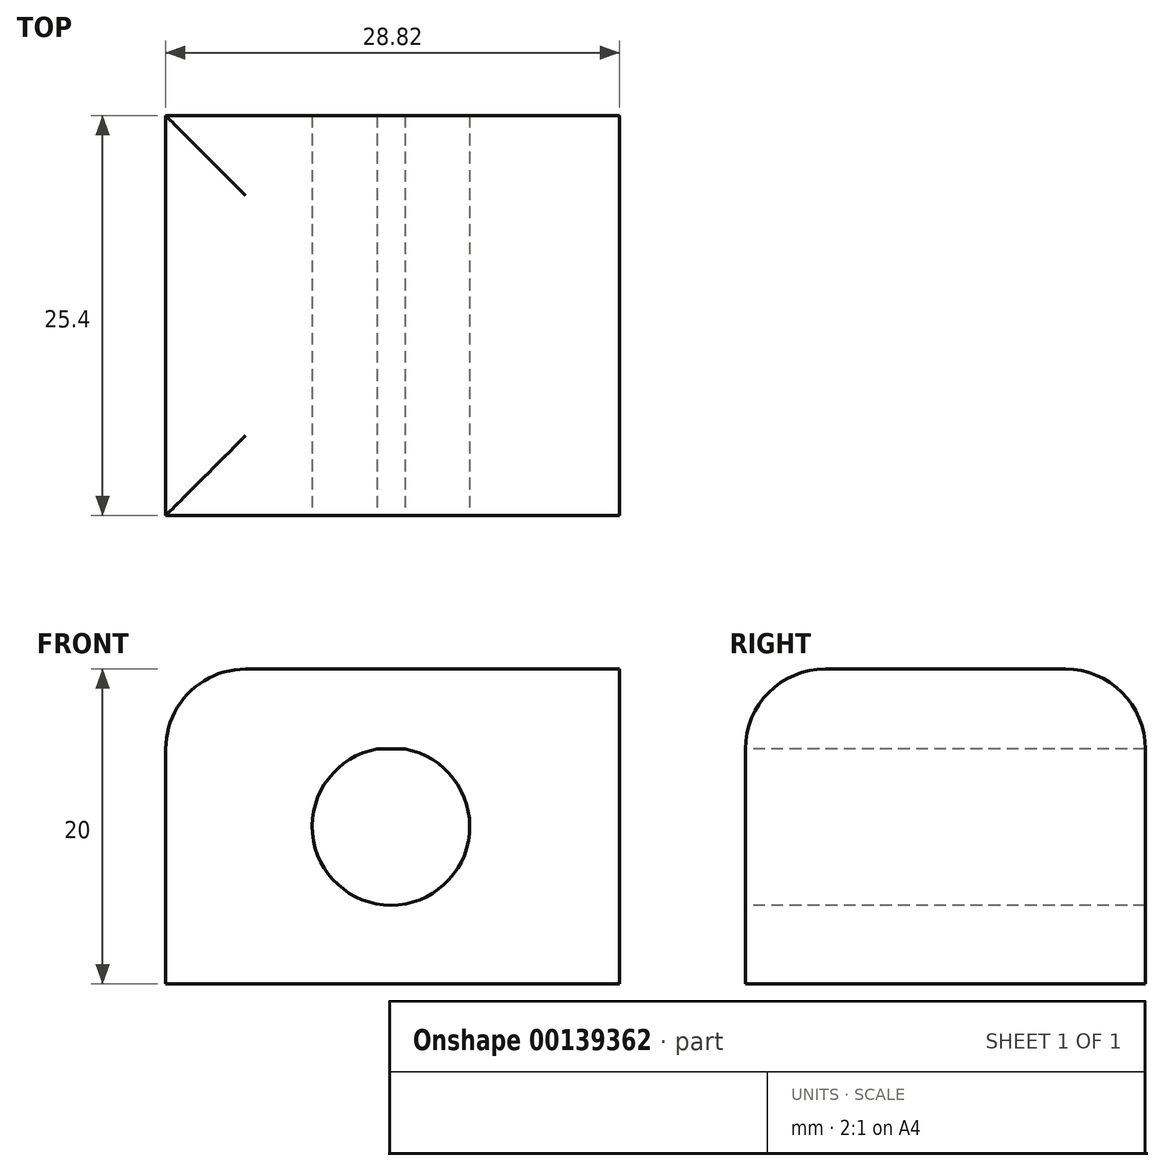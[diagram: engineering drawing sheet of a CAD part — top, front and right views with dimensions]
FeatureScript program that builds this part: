
annotation { "Feature Type Name" : "Feature", "Feature Type Description" : "" }
export const myFeature = defineFeature(function(context is Context, id is Id, definition is map)
    precondition{}
    {
        {
            var Q0;
            Q0=qCreatedBy(makeId("Front.planeOp"),FACE);
            var sketch = newSketch(context, id + "F0", { "sketchPlane" : qUnion([Q0])});
            skLineSegment(sketch, "E0.bottom", {"start": v(14.41, -10) * mm, "end": v(-14.41, -10) * mm});
            skLineSegment(sketch, "E0.top", {"start": v(14.41, 10) * mm, "end": v(-14.41, 10) * mm});
            skLineSegment(sketch, "E0.left", {"start": v(14.41, -10) * mm, "end": v(14.41, 10) * mm});
            skLineSegment(sketch, "E0.right", {"start": v(-14.41, -10) * mm, "end": v(-14.41, 10) * mm});
            skPoint(sketch, "E0.middle", {"position": v(0, 0) * mm});
            skSolve(sketch);
        }
        {
            var Q0;
            Q0=makeQuery(id+"F0.imprint","IMPRINT",FACE,{"disambiguationData":[TD([[makeQuery(id+"F0.imprint","IMPRINT",EDGE,{"derivedFrom":sQuery(id+"F0.wireOp",EDGE,"E0.bottom")}),-1.0]])]});
            extrude(context, id + "F1", {"entities" : qUnion([Q0]), "depth" : 25.4 * mm});
        }
        {
            var Q0;
            Q0=makeQuery(id+"F1.opExtrude","CAP_EDGE",EDGE,{"disambiguationData":[OSD([sQuery(id+"F0.wireOp",EDGE,"E0.top")])],"isStart":true});
            var Q1;
            Q1=makeQuery(id+"F1.opExtrude","SWEPT_EDGE",EDGE,{"disambiguationData":[OSD([sQuery(id+"F0.wireOp",EDGE,"E0.top"),sQuery(id+"F0.wireOp",EDGE,"E0.right")])]});
            var Q2;
            Q2=makeQuery(id+"F1.opExtrude","CAP_EDGE",EDGE,{"disambiguationData":[OSD([sQuery(id+"F0.wireOp",EDGE,"E0.top")])],"isStart":false});
            fillet(context, id + "F2", {"entities" : qUnion([Q0, Q1, Q2]), "radius" : 5.08 * mm, "tangentPropagation" : true, "allowEdgeOverflow" : false});
        }
        {
            var Q0;
            Q0=makeQuery(id+"F1.opExtrude","CAP_FACE",FACE,{"disambiguationData":[OSD([sQuery(id+"F0.wireOp",EDGE,"E0.bottom"),sQuery(id+"F0.wireOp",EDGE,"E0.top"),sQuery(id+"F0.wireOp",EDGE,"E0.left"),sQuery(id+"F0.wireOp",EDGE,"E0.right")])],"isStart":false});
            var Q1;
            Q1=makeQuery(id+"F1.opExtrude","CAP_FACE",FACE,{"disambiguationData":[OSD([sQuery(id+"F0.wireOp",EDGE,"E0.bottom"),sQuery(id+"F0.wireOp",EDGE,"E0.top"),sQuery(id+"F0.wireOp",EDGE,"E0.left"),sQuery(id+"F0.wireOp",EDGE,"E0.right")])],"isStart":false});
            var Q2;
            Q2=makeQuery(id+"F1.opExtrude","CAP_FACE",FACE,{"disambiguationData":[OSD([sQuery(id+"F0.wireOp",EDGE,"E0.bottom"),sQuery(id+"F0.wireOp",EDGE,"E0.top"),sQuery(id+"F0.wireOp",EDGE,"E0.left"),sQuery(id+"F0.wireOp",EDGE,"E0.right")])],"isStart":false});
            var sketch = newSketch(context, id + "F3", { "sketchPlane" : qUnion([Q0, Q1, Q2])});
            skCircle(sketch, "E1", {"center": v(-0.1, 0) * mm, "radius": 5 * mm});
            skSolve(sketch);
        }
        {
            var Q0;
            {var subQ0=sQuery(id+"F3.wireOp",EDGE,"E1");var subQ1=sQuery(id+"F0.wireOp",EDGE,"E0.top");var subQ2=makeQuery(id+"F2.opFillet","BLEND_EDGE",EDGE,{"blendedFrom":[makeQuery(id+"F1.opExtrude","CAP_EDGE",EDGE,{"disambiguationData":[OSD([subQ1])],"isStart":false}),makeQuery(id+"F1.opExtrude","CAP_FACE",FACE,{"disambiguationData":[OSD([sQuery(id+"F0.wireOp",EDGE,"E0.bottom"),subQ1,sQuery(id+"F0.wireOp",EDGE,"E0.left"),sQuery(id+"F0.wireOp",EDGE,"E0.right")])],"isStart":false})],"blendedInto":[makeQuery(id+"F1.opExtrude","CAP_FACE",FACE,{"disambiguationData":[OSD([sQuery(id+"F0.wireOp",EDGE,"E0.bottom"),subQ1,sQuery(id+"F0.wireOp",EDGE,"E0.left"),sQuery(id+"F0.wireOp",EDGE,"E0.right")])],"isStart":false})]});var subQ3=makeQuery(id+"F3.imprint","INTERSECT",VERTEX,{"disambiguationData":[OD(0.0)],"derivedFrom":[subQ2,subQ0]});Q0=makeQuery(id+"F3.imprint","IMPRINT",FACE,{"disambiguationData":[TD([[makeQuery(id+"F3.imprint","IMPRINT",EDGE,{"disambiguationData":[TD([[subQ3,-1.0]])],"derivedFrom":subQ0}),1.0]])]});}
            extrude(context, id + "F4", {"entities" : qUnion([Q0]), "operationType" : NewBodyOperationType.REMOVE, "endBound" : BoundingType.THROUGH_ALL, "oppositeDirection" : true, "depth" : 25 * mm});
        }
    });
